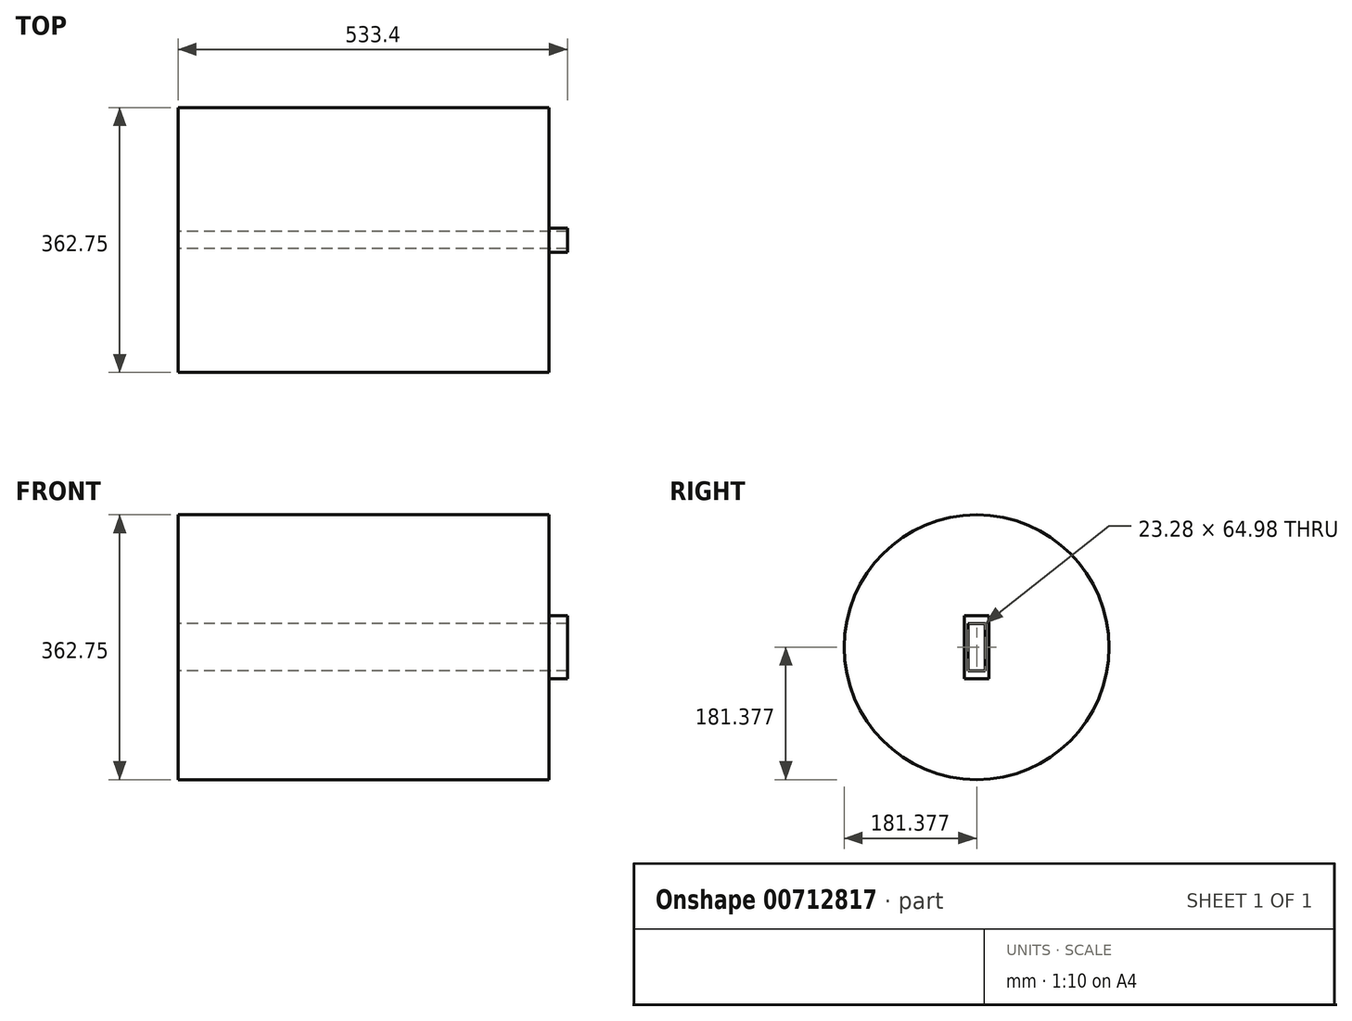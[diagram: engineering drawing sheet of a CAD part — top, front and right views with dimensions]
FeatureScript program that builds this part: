
annotation { "Feature Type Name" : "Feature", "Feature Type Description" : "" }
export const myFeature = defineFeature(function(context is Context, id is Id, definition is map)
    precondition{}
    {
        {
            var Q0;
            Q0=qCreatedBy(makeId("Right.planeOp"),FACE);
            var sketch = newSketch(context, id + "F0", { "sketchPlane" : qUnion([Q0])});
            skCircle(sketch, "E0", {"center": v(0.08, 1.12) * mm, "radius": 181.37 * mm});
            skLineSegment(sketch, "E1.bottom", {"start": v(11.71, 33.6) * mm, "end": v(-11.56, 33.6) * mm});
            skLineSegment(sketch, "E1.top", {"start": v(11.71, -31.37) * mm, "end": v(-11.56, -31.37) * mm});
            skLineSegment(sketch, "E1.left", {"start": v(11.71, 33.6) * mm, "end": v(11.71, -31.37) * mm});
            skLineSegment(sketch, "E1.right", {"start": v(-11.56, 33.6) * mm, "end": v(-11.56, -31.37) * mm});
            skLineSegment(sketch, "E2.bottom", {"start": v(16.7, 44.18) * mm, "end": v(-16.55, 44.18) * mm});
            skLineSegment(sketch, "E2.top", {"start": v(16.7, -41.94) * mm, "end": v(-16.55, -41.94) * mm});
            skLineSegment(sketch, "E2.left", {"start": v(16.7, 44.18) * mm, "end": v(16.7, -41.94) * mm});
            skLineSegment(sketch, "E2.right", {"start": v(-16.55, 44.18) * mm, "end": v(-16.55, -41.94) * mm});
            skSolve(sketch);
        }
        {
            var Q0;
            Q0=makeQuery(id+"F0.imprint","IMPRINT",FACE,{"disambiguationData":[TD([[makeQuery(id+"F0.imprint","IMPRINT",EDGE,{"derivedFrom":sQuery(id+"F0.wireOp",EDGE,"E1.bottom")}),-1.0]])]});
            extrude(context, id + "F1", {"entities" : qUnion([Q0]), "depth" : 533.4 * mm, "offsetDistance" : 25.4 * mm});
        }
        {
            var Q0;
            Q0=makeQuery(id+"F0.imprint","IMPRINT",FACE,{"disambiguationData":[TD([[makeQuery(id+"F0.imprint","IMPRINT",EDGE,{"derivedFrom":sQuery(id+"F0.wireOp",EDGE,"E0")}),1.0]])]});
            extrude(context, id + "F2", {"entities" : qUnion([Q0]), "operationType" : NewBodyOperationType.ADD, "depth" : 508 * mm, "offsetDistance" : 25.4 * mm});
        }
    });
